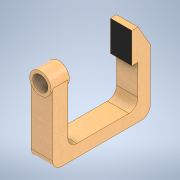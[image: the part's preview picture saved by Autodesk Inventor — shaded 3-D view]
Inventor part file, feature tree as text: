
AUTODESK INVENTOR PART (.ipt)
format: ipt  version: 2021 (Build 250183000, 183)  size: 171,008 bytes
history: native  units: mm
features: extrude x3, sketch x3, other x1, fillet x1, thread x1
ambient origin geometry x8: Origin, YZ Plane, XZ Plane, XY Plane, X Axis, Y Axis, Z Axis, Center Point
bodies: Body1 (feature_tree)
feature tree (9):
  other  "Sólido1"
  extrude  "Extrusão1"  Depth=70.0mm
  extrude  "Extrusão2"  Depth=5.0mm
  fillet  "Arredondamento1"  Radius=160.0mm
  extrude  "Extrusão3"  Depth=60.0mm
  thread  "Rosca1"  [1 undecoded]
  sketch  "Esboço1"  dims[d0=50.0mm d1=70.0mm]
  sketch  "Esboço2"  dims[d2=60.0mm d3=0.0mm d4=5.0mm d5=160.0mm]
  sketch  "Esboço3"  dims[d6=5.0mm d7=200.0mm d8=320.0mm d9=200.0mm d10=150.0deg d11=20.0mm d12=100.0mm d13=20.0mm d14=130.0mm d15=70.0mm d16=0.0mm d17=30.0mm d18=0.0mm d19=0.0mm d20=60.0mm d21=0.0mm]
note: 1 required parameter value undecoded (feature->parameter linkage not recoverable at this tier; creation-order binding heuristic only, values carry confidence <= 0.55)
